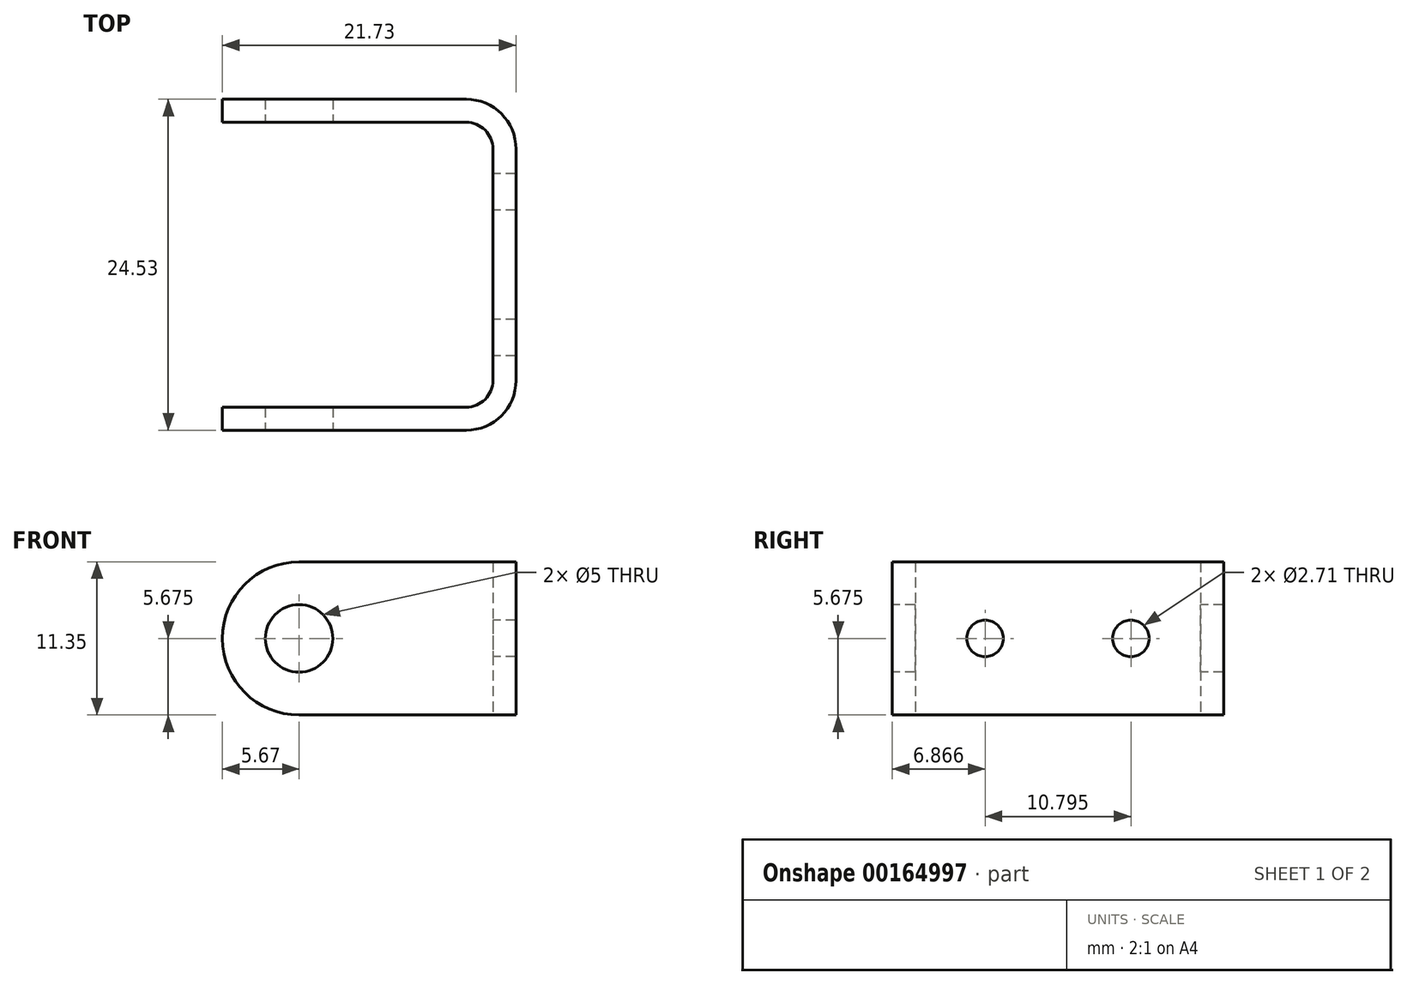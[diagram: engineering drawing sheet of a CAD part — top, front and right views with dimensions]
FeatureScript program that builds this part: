
annotation { "Feature Type Name" : "Feature", "Feature Type Description" : "" }
export const myFeature = defineFeature(function(context is Context, id is Id, definition is map)
    precondition{}
    {
        {
            var Q0;
            Q0=qCreatedBy(makeId("Top.planeOp"),FACE);
            var sketch = newSketch(context, id + "F0", { "sketchPlane" : qUnion([Q0])});
            skLineSegment(sketch, "E0.left", {"start": v(0, 0) * mm, "end": v(0, -21.11) * mm});
            skLineSegment(sketch, "E0.right", {"start": v(1.7, 1.7) * mm, "end": v(1.7, -22.82) * mm});
            skLineSegment(sketch, "E1.bottom", {"start": v(0, 0) * mm, "end": v(-20.02, 0) * mm});
            skLineSegment(sketch, "E1.top", {"start": v(1.7, 1.7) * mm, "end": v(-20.02, 1.7) * mm});
            skLineSegment(sketch, "E1.right", {"start": v(-20.02, 0) * mm, "end": v(-20.02, 1.7) * mm});
            skLineSegment(sketch, "E2.bottom", {"start": v(0, -21.11) * mm, "end": v(-20.02, -21.11) * mm});
            skLineSegment(sketch, "E2.top", {"start": v(1.7, -22.82) * mm, "end": v(-20.02, -22.82) * mm});
            skLineSegment(sketch, "E2.right", {"start": v(-20.02, -21.11) * mm, "end": v(-20.02, -22.82) * mm});
            skLineSegment(sketch, "E3", {"start": v(0, -10.56) * mm, "end": v(1.7, -10.56) * mm, "construction": true});
            skSolve(sketch);
        }
        {
            var Q0;
            Q0 = qSketchRegion(id + "F0", true);
            extrude(context, id + "F1", {"entities" : qUnion([Q0]), "depth" : 11.35 * mm});
        }
        {
            var Q0;
            Q0=makeQuery(id+"F1.opExtrude","CAP_EDGE",EDGE,{"disambiguationData":[OSD([sQuery(id+"F0.wireOp",EDGE,"E2.right")])],"isStart":false});
            var Q1;
            Q1=makeQuery(id+"F1.opExtrude","CAP_EDGE",EDGE,{"disambiguationData":[OSD([sQuery(id+"F0.wireOp",EDGE,"E2.right")])],"isStart":true});
            var Q2;
            Q2=makeQuery(id+"F1.opExtrude","CAP_EDGE",EDGE,{"disambiguationData":[OSD([sQuery(id+"F0.wireOp",EDGE,"E1.right")])],"isStart":false});
            var Q3;
            Q3=makeQuery(id+"F1.opExtrude","CAP_EDGE",EDGE,{"disambiguationData":[OSD([sQuery(id+"F0.wireOp",EDGE,"E1.right")])],"isStart":true});
            fillet(context, id + "F2", {"entities" : qUnion([Q0, Q1, Q2, Q3]), "radius" : 5.67 * mm, "tangentPropagation" : true, "allowEdgeOverflow" : false});
        }
        {
            var Q0;
            Q0=makeQuery(id+"F1.opExtrude","SWEPT_FACE",FACE,{"disambiguationData":[OSD([sQuery(id+"F0.wireOp",EDGE,"E2.top")])]});
            var sketch = newSketch(context, id + "F3", { "sketchPlane" : qUnion([Q0])});
            skCircle(sketch, "E4", {"center": v(-14.35, 5.67) * mm, "radius": 2.5 * mm});
            skSolve(sketch);
        }
        {
            var Q0;
            Q0 = qSketchRegion(id + "F3", true);
            var Q1;
            Q1=makeQuery(id+"F1.opExtrude","SWEPT_FACE",FACE,{"disambiguationData":[OSD([sQuery(id+"F0.wireOp",EDGE,"E1.top")])]});
            extrude(context, id + "F4", {"entities" : qUnion([Q0]), "operationType" : NewBodyOperationType.REMOVE, "endBound" : BoundingType.UP_TO_SURFACE, "oppositeDirection" : true, "endBoundEntityFace" : qUnion([Q1]), "depth" : 25.4 * mm});
        }
        {
            var Q0;
            Q0=makeQuery(id+"F1.opExtrude","SWEPT_EDGE",EDGE,{"disambiguationData":[OSD([sQuery(id+"F0.wireOp",EDGE,"E0.right"),sQuery(id+"F0.wireOp",EDGE,"E2.top")])]});
            var Q1;
            Q1=makeQuery(id+"F1.opExtrude","SWEPT_EDGE",EDGE,{"disambiguationData":[OSD([sQuery(id+"F0.wireOp",EDGE,"E0.right"),sQuery(id+"F0.wireOp",EDGE,"E1.top")])]});
            fillet(context, id + "F5", {"entities" : qUnion([Q0, Q1]), "radius" : 3.7 * mm, "tangentPropagation" : true, "allowEdgeOverflow" : false});
        }
        {
            var Q0;
            Q0=makeQuery(id+"F1.opExtrude","SWEPT_EDGE",EDGE,{"disambiguationData":[OSD([sQuery(id+"F0.wireOp",EDGE,"E0.left"),sQuery(id+"F0.wireOp",EDGE,"E2.bottom")])]});
            var Q1;
            Q1=makeQuery(id+"F1.opExtrude","SWEPT_EDGE",EDGE,{"disambiguationData":[OSD([sQuery(id+"F0.wireOp",EDGE,"E0.left"),sQuery(id+"F0.wireOp",EDGE,"E1.bottom")])]});
            fillet(context, id + "F6", {"entities" : qUnion([Q0, Q1]), "radius" : 1.98 * mm, "tangentPropagation" : true, "allowEdgeOverflow" : false});
        }
        {
            var Q0;
            Q0=makeQuery(id+"F1.opExtrude","SWEPT_FACE",FACE,{"disambiguationData":[OSD([sQuery(id+"F0.wireOp",EDGE,"E0.left")])]});
            var sketch = newSketch(context, id + "F7", { "sketchPlane" : qUnion([Q0])});
            skLineSegment(sketch, "E5", {"start": v(19.13, 5.67) * mm, "end": v(15.95, 5.67) * mm, "construction": true});
            skLineSegment(sketch, "E6", {"start": v(1.98, 5.67) * mm, "end": v(5.16, 5.67) * mm, "construction": true});
            skCircle(sketch, "E7", {"center": v(15.95, 5.67) * mm, "radius": 1.35 * mm});
            skCircle(sketch, "E8", {"center": v(5.16, 5.67) * mm, "radius": 1.35 * mm});
            skSolve(sketch);
        }
        {
            var Q0;
            Q0 = qSketchRegion(id + "F7", true);
            var Q1;
            Q1=makeQuery(id+"F1.opExtrude","SWEPT_FACE",FACE,{"disambiguationData":[OSD([sQuery(id+"F0.wireOp",EDGE,"E0.right")])]});
            extrude(context, id + "F8", {"entities" : qUnion([Q0]), "operationType" : NewBodyOperationType.REMOVE, "endBound" : BoundingType.UP_TO_SURFACE, "oppositeDirection" : true, "endBoundEntityFace" : qUnion([Q1]), "depth" : 25.4 * mm});
        }
    });
